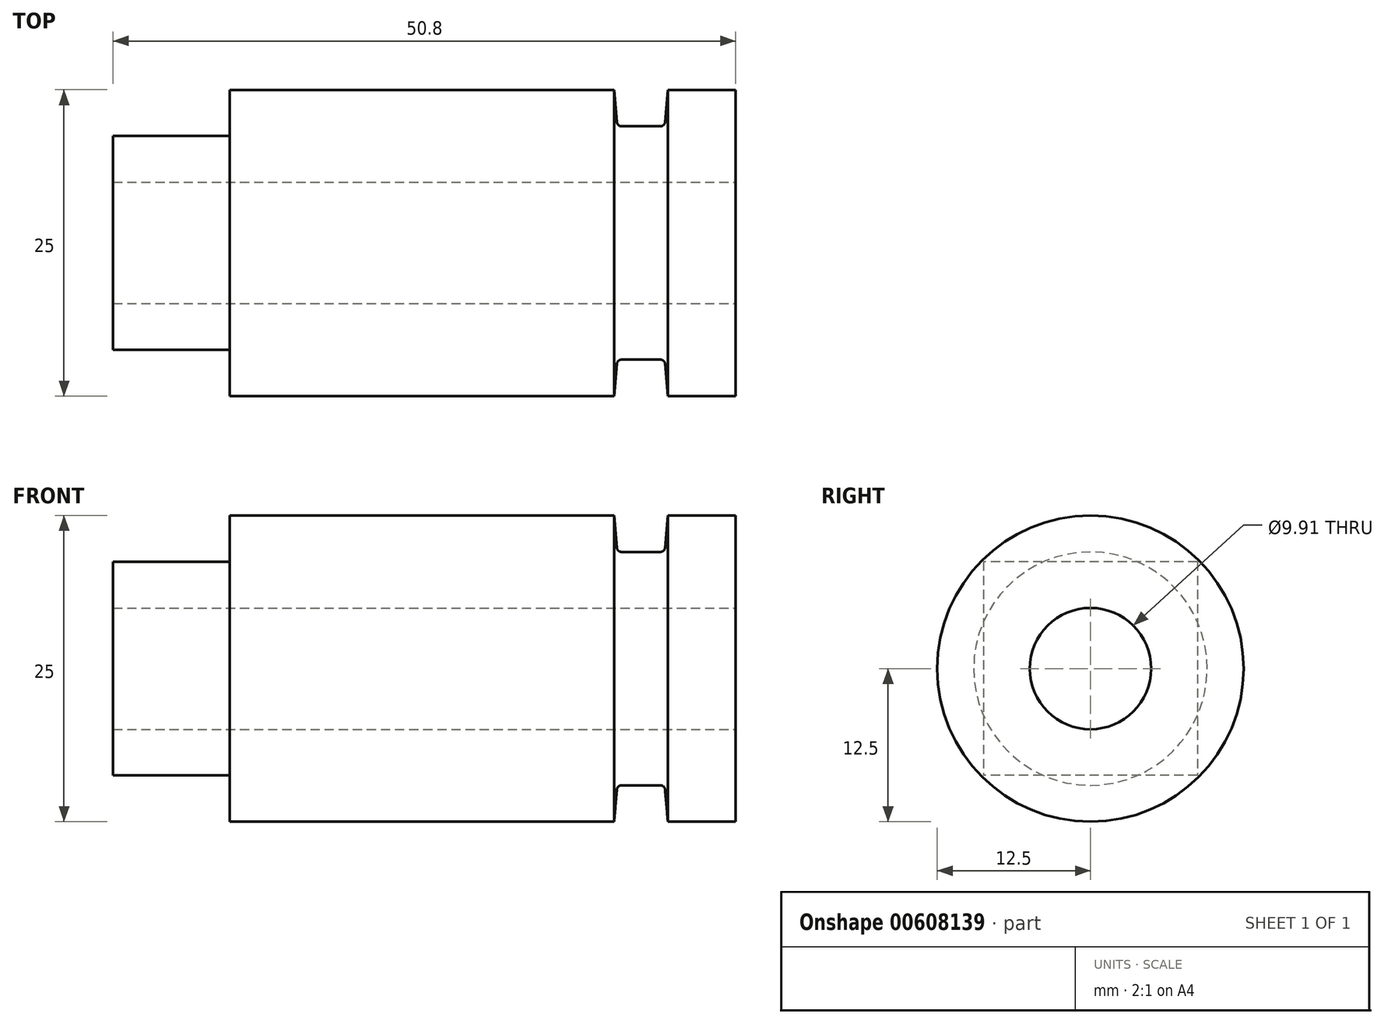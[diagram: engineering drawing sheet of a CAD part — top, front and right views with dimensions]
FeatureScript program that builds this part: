
annotation { "Feature Type Name" : "Feature", "Feature Type Description" : "" }
export const myFeature = defineFeature(function(context is Context, id is Id, definition is map)
    precondition{}
    {
        {
            var Q0;
            Q0=qCreatedBy(makeId("Front.planeOp"),FACE);
            var sketch = newSketch(context, id + "F0", { "sketchPlane" : qUnion([Q0])});
            skLineSegment(sketch, "E0", {"start": v(0, 0) * mm, "end": v(-41.9, 0) * mm, "construction": true});
            skLineSegment(sketch, "E1", {"start": v(0, 4.95) * mm, "end": v(-41.28, 4.95) * mm});
            skLineSegment(sketch, "E2", {"start": v(-41.28, 4.95) * mm, "end": v(-41.28, 12.5) * mm});
            skLineSegment(sketch, "E3", {"start": v(-41.28, 12.5) * mm, "end": v(-9.93, 12.5) * mm});
            skLineSegment(sketch, "E4", {"start": v(-5.54, 12.5) * mm, "end": v(0, 12.5) * mm});
            skLineSegment(sketch, "E5", {"start": v(0, 12.5) * mm, "end": v(0, 4.95) * mm});
            skLineSegment(sketch, "E6", {"start": v(-9.93, 12.5) * mm, "end": v(-9.7, 9.87) * mm});
            skLineSegment(sketch, "E7", {"start": v(-9.32, 9.53) * mm, "end": v(-6.15, 9.53) * mm});
            skLineSegment(sketch, "E8", {"start": v(-5.77, 9.87) * mm, "end": v(-5.54, 12.5) * mm});
            skPoint(sketch, "E9.visualSharp", {"position": v(-9.67, 9.53) * mm});
            skArc(sketch, "E9.filletArc", {"start": v(-9.7, 9.87) * mm, "mid": v(-9.58, 9.63) * mm, "end": v(-9.32, 9.53) * mm});
            skPoint(sketch, "E10.visualSharp", {"position": v(-5.8, 9.53) * mm});
            skArc(sketch, "E10.filletArc", {"start": v(-6.15, 9.53) * mm, "mid": v(-5.89, 9.63) * mm, "end": v(-5.77, 9.87) * mm});
            skSolve(sketch);
        }
        {
            var Q0;
            Q0=makeQuery(id+"F0.imprint","IMPRINT",FACE,{"disambiguationData":[TD([[makeQuery(id+"F0.imprint","IMPRINT",EDGE,{"derivedFrom":sQuery(id+"F0.wireOp",EDGE,"E1")}),-1.0]])]});
            var Q1;
            Q1=sQuery(id+"F0.wireOp",EDGE,"E0");
            revolve(context, id + "F1", {"entities" : qUnion([Q0]), "axis" : qUnion([Q1]), "revolveType" : RevolveType.FULL});
        }
        {
            var Q0;
            Q0=makeQuery(id+"F1.opRevolve","SWEPT_FACE",FACE,{"disambiguationData":[OSD([sQuery(id+"F0.wireOp",EDGE,"E2")])]});
            var sketch = newSketch(context, id + "F2", { "sketchPlane" : qUnion([Q0])});
            skLineSegment(sketch, "E11.bottom", {"start": v(-8.72, 8.72) * mm, "end": v(8.72, 8.72) * mm});
            skLineSegment(sketch, "E11.top", {"start": v(-8.72, -8.72) * mm, "end": v(8.72, -8.72) * mm});
            skLineSegment(sketch, "E11.left", {"start": v(-8.72, 8.72) * mm, "end": v(-8.72, -8.72) * mm});
            skLineSegment(sketch, "E11.right", {"start": v(8.72, 8.72) * mm, "end": v(8.72, -8.72) * mm});
            skSolve(sketch);
        }
        {
            var Q0;
            Q0=makeQuery(id+"F2.imprint","IMPRINT",FACE,{"disambiguationData":[TD([[makeQuery(id+"F2.imprint","IMPRINT",EDGE,{"derivedFrom":sQuery(id+"F2.wireOp",EDGE,"E11.bottom")}),-1.0]])]});
            extrude(context, id + "F3", {"entities" : qUnion([Q0]), "operationType" : NewBodyOperationType.ADD, "depth" : 9.52 * mm, "offsetDistance" : 25.4 * mm});
        }
    });
